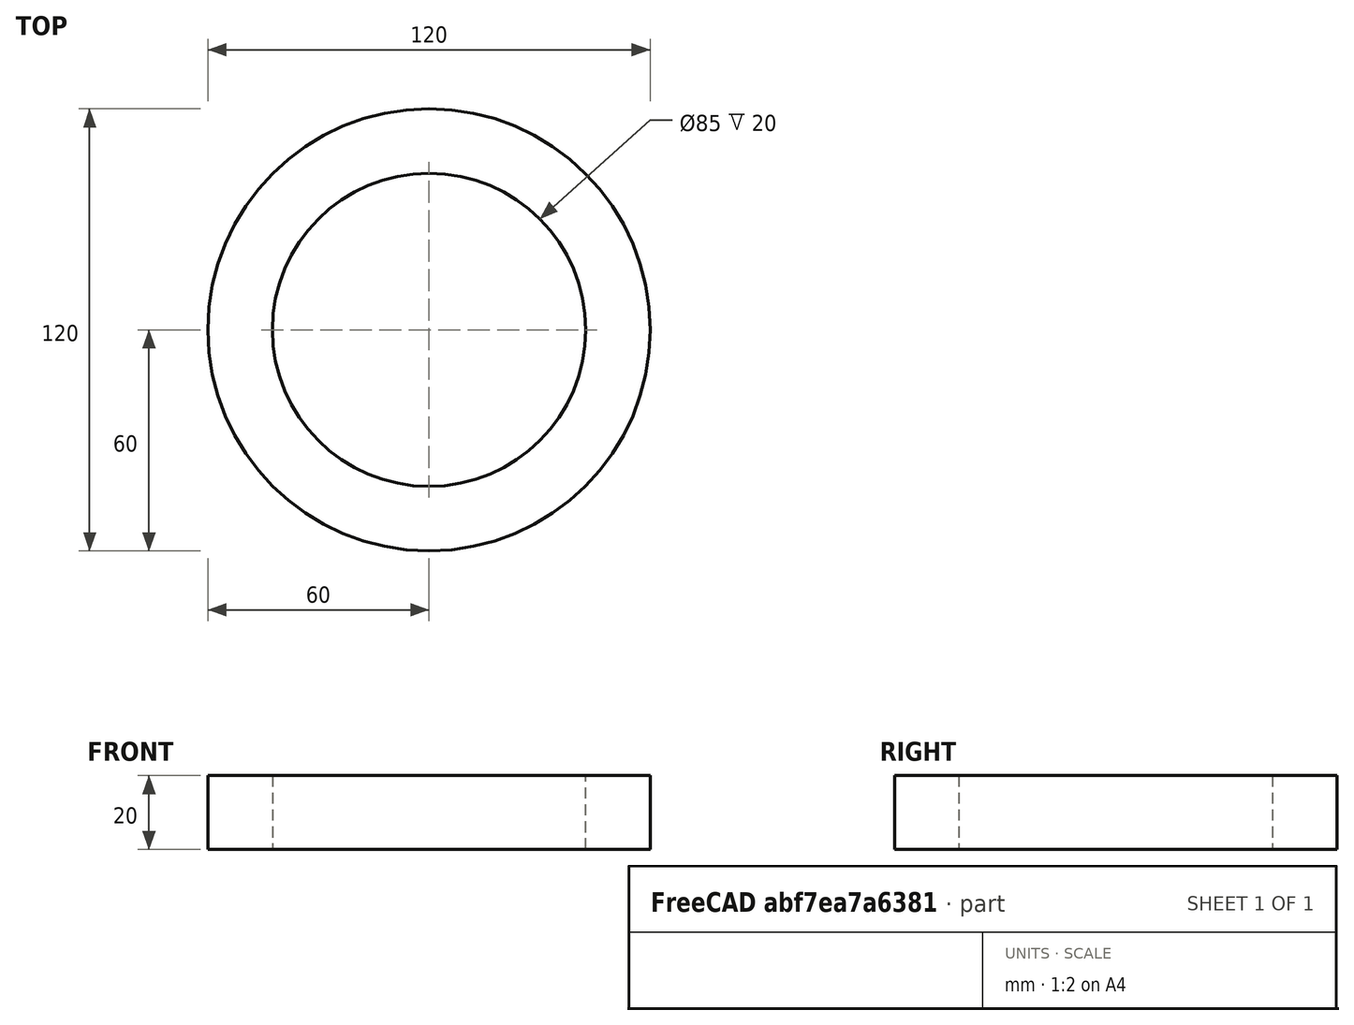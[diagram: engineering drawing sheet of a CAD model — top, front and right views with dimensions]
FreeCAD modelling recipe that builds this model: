
FCSTD DOCUMENT  (FreeCAD 0.19R24276 (Git))
Label: Stripe_coil_20mm
License: All rights reserved
LicenseURL: http://en.wikipedia.org/wiki/All_rights_reserved
objects: Sketcher::SketchObject×1, PartDesign::Pad×1, PartDesign::Body×1
note: 4 computed .brp shape members not serialized (recipe doc carries the construction recipe); baked Part::Feature solids carry a one-line shape summary decoded from their .brp

FEATURE [Sketcher::SketchObject] Sketch
  FullyConstrained = true
  MapMode = 5
  Support = -> [XY_Plane]
  sketch-geometry (2):
    g0: Circle CenterX=0 CenterY=0 CenterZ=0 NormalX=0 NormalY=0 NormalZ=1 AngleXU=0 Radius=42.5
    g1: Circle CenterX=0 CenterY=0 CenterZ=0 NormalX=0 NormalY=0 NormalZ=1 AngleXU=0 Radius=60
  constraints (4):
    c: Coincident(g0,g-1)
    c: Coincident(g1,g0)
    c: Diameter(g0) = 85
    c: Diameter(g1) = 120
FEATURE [PartDesign::Pad] Pad
  Direction = (1,1,1)
  Length = 20
  Length2 = 100
  Profile = -> Sketch
  Type = 0
FEATURE [PartDesign::Body] Body
  Group = -> [Sketch,Pad]
  Origin = -> Origin
  Tip = -> Pad
